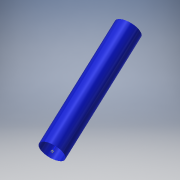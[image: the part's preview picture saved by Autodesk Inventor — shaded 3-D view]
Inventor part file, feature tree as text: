
AUTODESK INVENTOR PART (.ipt)
format: ipt  version: 2019.2 (Build 232265000, 265)  size: 124,928 bytes
history: native  units: mm (DEFAULTED — no unit token found)
features: other x4, plane x1, sketch x1, sweep x1
ambient origin geometry x8: Origin, YZ Plane, XZ Plane, XY Plane, X Axis, Y Axis, Z Axis, Center Point
bodies: Body1 (feature_tree)
feature tree (7):
  other  "Work Point1"
  other  "Work Point2"
  other  "Segment1"
  plane  "Work Plane1"
  sketch  "Sketch1"  dims[d0=0.0mm d1=0.0mm]
  other  "Srf1"
  sweep  "SweepSrf1"
